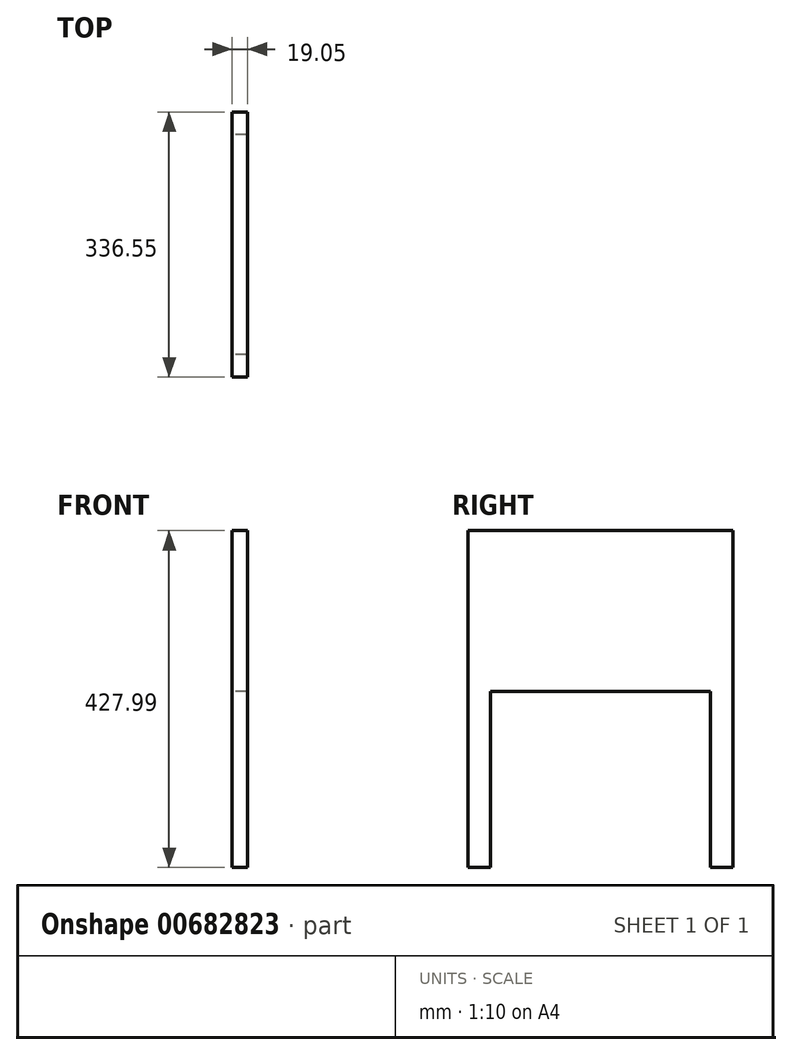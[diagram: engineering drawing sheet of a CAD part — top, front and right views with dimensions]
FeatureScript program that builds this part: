
annotation { "Feature Type Name" : "Feature", "Feature Type Description" : "" }
export const myFeature = defineFeature(function(context is Context, id is Id, definition is map)
    precondition{}
    {
        {
            var Q0;
            Q0=qCreatedBy(makeId("Right.planeOp"),FACE);
            var sketch = newSketch(context, id + "F0", { "sketchPlane" : qUnion([Q0])});
            skLineSegment(sketch, "E0.bottom", {"start": v(0, 0) * mm, "end": v(-28.57, 0) * mm});
            skLineSegment(sketch, "E0.top", {"start": v(0, 428) * mm, "end": v(-336.55, 428) * mm});
            skLineSegment(sketch, "E0.left", {"start": v(0, 0) * mm, "end": v(0, 428) * mm});
            skLineSegment(sketch, "E0.right", {"start": v(-336.55, 0) * mm, "end": v(-336.55, 428) * mm});
            skLineSegment(sketch, "E1", {"start": v(-307.98, 0) * mm, "end": v(-307.98, 223.52) * mm});
            skLineSegment(sketch, "E2", {"start": v(-307.98, 223.52) * mm, "end": v(-28.57, 223.52) * mm});
            skLineSegment(sketch, "E3", {"start": v(-28.57, 223.52) * mm, "end": v(-28.57, 0) * mm});
            skLineSegment(sketch, "E4.trimOffspring", {"start": v(-307.98, 0) * mm, "end": v(-336.55, 0) * mm});
            skSolve(sketch);
        }
        {
            var Q0;
            Q0=qSketchRegion(id+"F0",true);
            extrude(context, id + "F1", {"entities" : qUnion([Q0]), "depth" : 19.05 * mm, "offsetDistance" : 25.4 * mm});
        }
    });
